# Revit family: QF_BOURGEAT_plaque_de_decoupe_aluminium
name_source: partatom
category: Equipement spécialisé
revit_build: Autodesk Revit 2015 (Build: 20140606_1530(x64)
units: mm (PartAtom-declared; Revit-internal decimal feet)

## types (2) — shared parameters
Charge max = 10.00 kg
Fabricant = BOURGEAT
Fréquence = 50 Hz
Indice de protection = 21
Intensité nominale = 1 A
Phase = 2
Poids net à vide = 4.50 kg
Puissance électrique  = 330 W
Spécification du Fabricant = PLAQUE MODULO
Tension = 230 V
URL catalogue = http://www.bourgeat.fr

## per-type parameters (varying)
| type | Hauteur hors tout | Longueur hors tout | Modèle | Profondeur hors tout | support_empilable |
| plaque_decoupe_alu | 65 mm  [stored 0.213255 ft] | 545 mm  [stored 1.78806 ft] | 875003 | 345 mm  [stored 1.13189 ft] | Non |
| plaque_decoupe_alu+support | 150 mm | 620 mm  [stored 2.03412 ft] | 875003 + 875000 | 350 mm  [stored 1.14829 ft] | Oui |

note: [stored X ft] marks values corroborated as IEEE doubles in the binary element streams (Revit-internal decimal feet)
